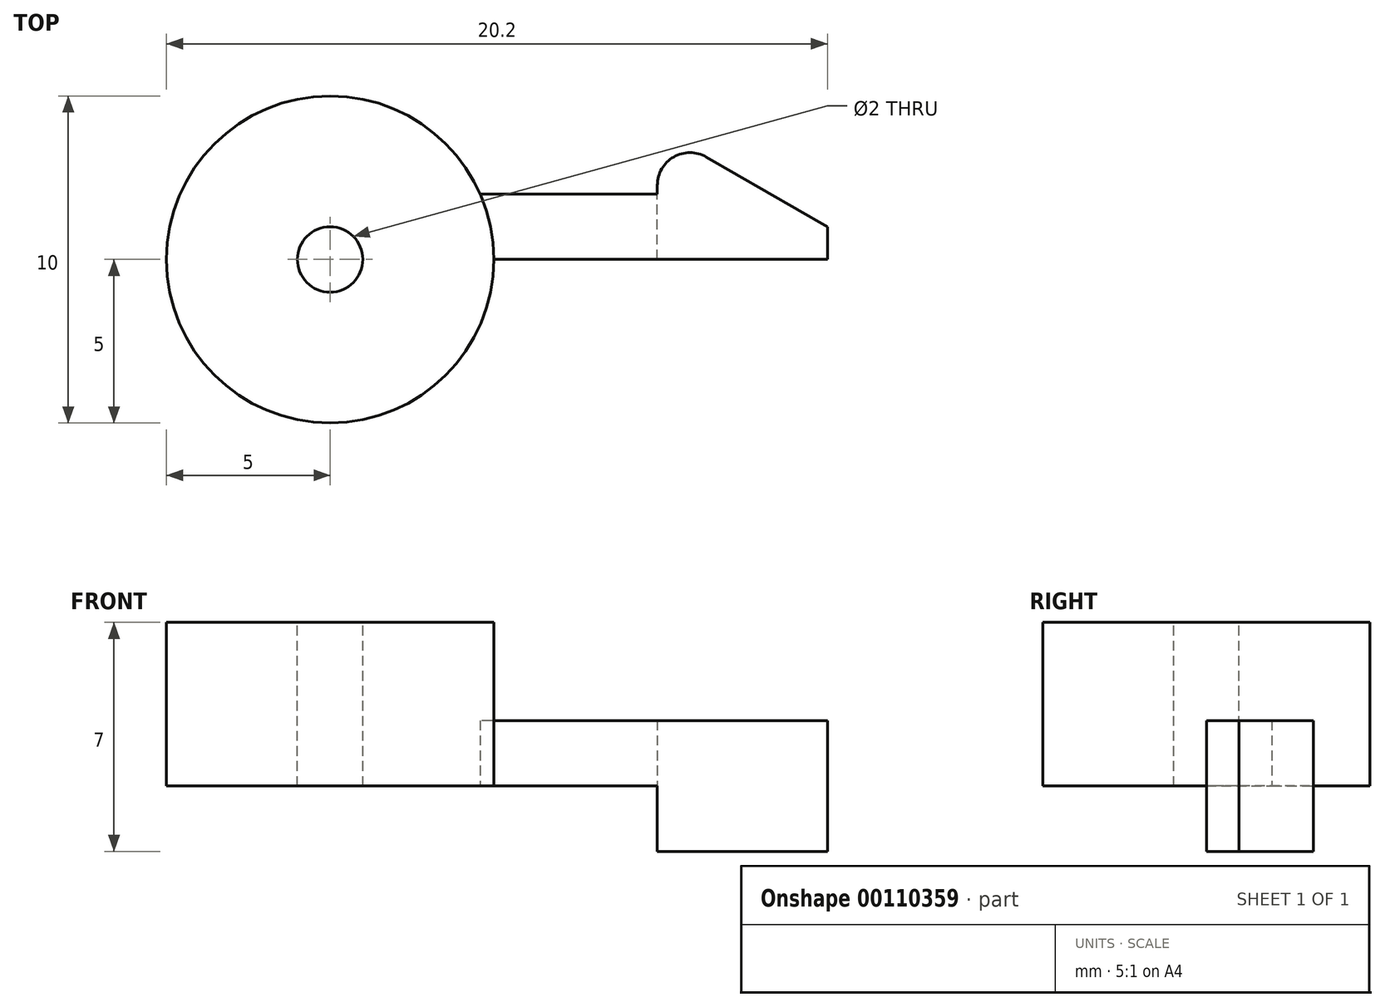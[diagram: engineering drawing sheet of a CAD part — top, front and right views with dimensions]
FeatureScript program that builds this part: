
annotation { "Feature Type Name" : "Feature", "Feature Type Description" : "" }
export const myFeature = defineFeature(function(context is Context, id is Id, definition is map)
    precondition{}
    {
        {
            var Q0;
            Q0=qCreatedBy(makeId("Top.planeOp"),FACE);
            var sketch = newSketch(context, id + "F0", { "sketchPlane" : qUnion([Q0])});
            skCircle(sketch, "E0", {"center": v(0, 0) * mm, "radius": 5 * mm});
            skLineSegment(sketch, "E1", {"start": v(5, 0) * mm, "end": v(10, 0) * mm});
            skLineSegment(sketch, "E2", {"start": v(10, 0) * mm, "end": v(10, 2) * mm});
            skLineSegment(sketch, "E3", {"start": v(10, 2) * mm, "end": v(4.58, 2) * mm});
            skLineSegment(sketch, "E4", {"start": v(10, 2) * mm, "end": v(10, 4) * mm});
            skLineSegment(sketch, "E5", {"start": v(10, 0) * mm, "end": v(15.2, 0) * mm});
            skLineSegment(sketch, "E6", {"start": v(15.2, 0) * mm, "end": v(15.2, 1) * mm});
            skLineSegment(sketch, "E7", {"start": v(10, 4) * mm, "end": v(15.2, 1) * mm});
            skSolve(sketch);
        }
        {
            var Q0;
            {var subQ0=sQuery(id+"F0.wireOp",EDGE,"E1");Q0=makeQuery(id+"F0.imprint","IMPRINT",FACE,{"disambiguationData":[TD([[makeQuery(id+"F0.imprint","IMPRINT",EDGE,{"derivedFrom":subQ0}),1.0]])]});}
            extrude(context, id + "F1", {"entities" : qUnion([Q0]), "depth" : 2 * mm});
        }
        {
            var Q0;
            {var subQ0=sQuery(id+"F0.wireOp",EDGE,"E0");var subQ1=makeQuery(id+"F0.imprint","INTERSECT",VERTEX,{"derivedFrom":[subQ0,sQuery(id+"F0.wireOp",EDGE,"E1")]});Q0=makeQuery(id+"F0.imprint","IMPRINT",FACE,{"disambiguationData":[TD([[makeQuery(id+"F0.imprint","IMPRINT",EDGE,{"disambiguationData":[TD([[subQ1,-1.0]])],"derivedFrom":subQ0}),1.0]])]});}
            extrude(context, id + "F2", {"entities" : qUnion([Q0]), "operationType" : NewBodyOperationType.ADD, "depth" : 5 * mm});
        }
        {
            var Q0;
            Q0=makeQuery(id+"F0.imprint","IMPRINT",FACE,{"disambiguationData":[TD([[makeQuery(id+"F0.imprint","IMPRINT",EDGE,{"derivedFrom":sQuery(id+"F0.wireOp",EDGE,"E2")}),-1.0]])]});
            extrude(context, id + "F3", {"entities" : qUnion([Q0]), "operationType" : NewBodyOperationType.ADD, "depth" : 4 * mm, "symmetric" : true});
        }
        {
            var Q0;
            Q0=makeQuery(id+"F3.opExtrude","SWEPT_EDGE",EDGE,{"disambiguationData":[OSD([sQuery(id+"F0.wireOp",EDGE,"E4"),sQuery(id+"F0.wireOp",EDGE,"E7")])]});
            fillet(context, id + "F4", {"entities" : qUnion([Q0]), "radius" : 1 * mm, "tangentPropagation" : true, "allowEdgeOverflow" : false});
        }
        {
            var Q0;
            Q0=sQuery(id+"F0.wireOp",VERTEX,"E0.center");
            var Q1;
            Q1=makeQuery(id+"F1.opExtrude","SWEPT_BODY",BODY,{"disambiguationData":[OSD([sQuery(id+"F0.wireOp",EDGE,"E0"),sQuery(id+"F0.wireOp",EDGE,"E1"),sQuery(id+"F0.wireOp",EDGE,"E2"),sQuery(id+"F0.wireOp",EDGE,"E3")])]});
            hole(context, id + "F5", {"style" : HoleStyle.SIMPLE, "endStyle" : HoleEndStyle.THROUGH, "oppositeDirection" : true, "holeDiameter" : 2 * mm, "locations" : qUnion([Q0]), "scope" : qUnion([Q1]), "isTappedThrough" : true});
        }
    });
